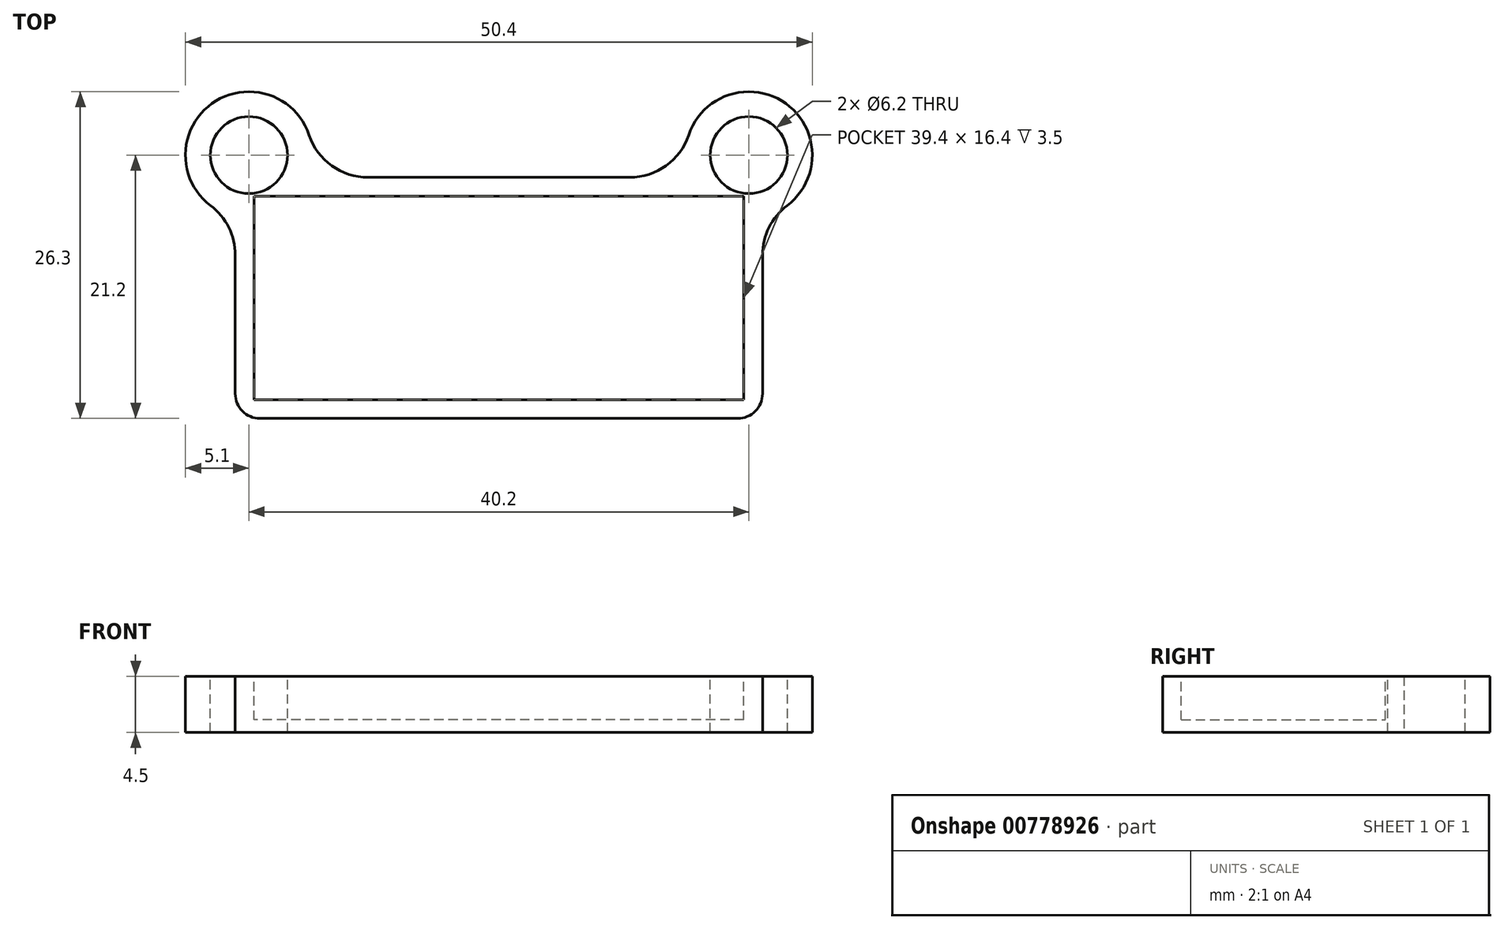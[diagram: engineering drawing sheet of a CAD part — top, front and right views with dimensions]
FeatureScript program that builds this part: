
annotation { "Feature Type Name" : "Feature", "Feature Type Description" : "" }
export const myFeature = defineFeature(function(context is Context, id is Id, definition is map)
    precondition{}
    {
        {
            var Q0;
            Q0=qCreatedBy(makeId("Top.planeOp"),FACE);
            var sketch = newSketch(context, id + "F0", { "sketchPlane" : qUnion([Q0])});
            skCircle(sketch, "E0", {"center": v(-20.1, 0) * mm, "radius": 3.1 * mm});
            skCircle(sketch, "E1", {"center": v(20.1, 0) * mm, "radius": 3.1 * mm});
            skLineSegment(sketch, "E2", {"start": v(-20.1, 0) * mm, "end": v(20.1, 0) * mm});
            skLineSegment(sketch, "E3.bottom", {"start": v(19.7, -19.7) * mm, "end": v(-19.7, -19.7) * mm});
            skLineSegment(sketch, "E3.top", {"start": v(19.7, -3.3) * mm, "end": v(-19.7, -3.3) * mm});
            skLineSegment(sketch, "E3.left", {"start": v(19.7, -19.7) * mm, "end": v(19.7, -3.3) * mm});
            skLineSegment(sketch, "E3.right", {"start": v(-19.7, -19.7) * mm, "end": v(-19.7, -3.3) * mm});
            skPoint(sketch, "E3.middle", {"position": v(0, -11.5) * mm});
            skLineSegment(sketch, "E4", {"start": v(0, 0) * mm, "end": v(0, -11.5) * mm, "construction": true});
            skSolve(sketch);
        }
        {
            var Q0;
            Q0=qCreatedBy(makeId("Top.planeOp"),FACE);
            var sketch = newSketch(context, id + "F1", { "sketchPlane" : qUnion([Q0])});
            skLineSegment(sketch, "E5.0", {"start": v(21.2, -1.8) * mm, "end": v(-21.2, -1.8) * mm});
            skLineSegment(sketch, "E5.1", {"start": v(21.2, -21.2) * mm, "end": v(21.2, -1.8) * mm});
            skLineSegment(sketch, "E5.2", {"start": v(21.2, -21.2) * mm, "end": v(-21.2, -21.2) * mm});
            skLineSegment(sketch, "E5.3", {"start": v(-21.2, -21.2) * mm, "end": v(-21.2, -1.8) * mm});
            skCircle(sketch, "E6.0", {"center": v(-20.1, 0) * mm, "radius": 5.1 * mm});
            skCircle(sketch, "E7.0", {"center": v(20.1, 0) * mm, "radius": 5.1 * mm});
            skSolve(sketch);
        }
        {
            var Q0;
            {var subQ0=sQuery(id+"F1.wireOp",EDGE,"E5.3");var subQ1=sQuery(id+"F1.wireOp",EDGE,"E5.0");var subQ2=makeQuery(id+"F1.imprint","INTERSECT",VERTEX,{"derivedFrom":[subQ1,subQ0]});Q0=makeQuery(id+"F1.imprint","IMPRINT",FACE,{"disambiguationData":[TD([[makeQuery(id+"F1.imprint","IMPRINT",EDGE,{"disambiguationData":[TD([[subQ2,1.0]])],"derivedFrom":subQ1}),-1.0]])]});}
            var Q1;
            {var subQ0=sQuery(id+"F1.wireOp",EDGE,"E5.2");Q1=makeQuery(id+"F1.imprint","IMPRINT",FACE,{"disambiguationData":[TD([[makeQuery(id+"F1.imprint","IMPRINT",EDGE,{"derivedFrom":subQ0}),-1.0]])]});}
            var Q2;
            {var subQ0=sQuery(id+"F1.wireOp",EDGE,"E5.1");var subQ1=sQuery(id+"F1.wireOp",EDGE,"E5.0");var subQ2=makeQuery(id+"F1.imprint","INTERSECT",VERTEX,{"derivedFrom":[subQ1,subQ0]});Q2=makeQuery(id+"F1.imprint","IMPRINT",FACE,{"disambiguationData":[TD([[makeQuery(id+"F1.imprint","IMPRINT",EDGE,{"disambiguationData":[TD([[subQ2,-1.0]])],"derivedFrom":subQ1}),-1.0]])]});}
            var Q3;
            {var subQ0=sQuery(id+"F1.wireOp",EDGE,"E5.1");var subQ1=sQuery(id+"F1.wireOp",EDGE,"E5.0");var subQ2=makeQuery(id+"F1.imprint","INTERSECT",VERTEX,{"derivedFrom":[subQ1,subQ0]});Q3=makeQuery(id+"F1.imprint","IMPRINT",FACE,{"disambiguationData":[TD([[makeQuery(id+"F1.imprint","IMPRINT",EDGE,{"disambiguationData":[TD([[subQ2,-1.0]])],"derivedFrom":subQ1}),1.0]])]});}
            var Q4;
            {var subQ0=sQuery(id+"F1.wireOp",EDGE,"E5.3");var subQ1=sQuery(id+"F1.wireOp",EDGE,"E5.0");var subQ2=makeQuery(id+"F1.imprint","INTERSECT",VERTEX,{"derivedFrom":[subQ1,subQ0]});Q4=makeQuery(id+"F1.imprint","IMPRINT",FACE,{"disambiguationData":[TD([[makeQuery(id+"F1.imprint","IMPRINT",EDGE,{"disambiguationData":[TD([[subQ2,1.0]])],"derivedFrom":subQ1}),1.0]])]});}
            extrude(context, id + "F2", {"entities" : qUnion([Q0, Q1, Q2, Q3, Q4]), "oppositeDirection" : true, "depth" : 4.5 * mm, "offsetDistance" : 25 * mm});
        }
        {
            var Q0;
            Q0=makeQuery(id+"F0.imprint","IMPRINT",FACE,{"disambiguationData":[TD([[makeQuery(id+"F0.imprint","IMPRINT",EDGE,{"derivedFrom":sQuery(id+"F0.wireOp",EDGE,"E0")}),1.0]])]});
            var Q1;
            Q1=makeQuery(id+"F0.imprint","IMPRINT",FACE,{"disambiguationData":[TD([[makeQuery(id+"F0.imprint","IMPRINT",EDGE,{"derivedFrom":sQuery(id+"F0.wireOp",EDGE,"E1")}),1.0]])]});
            extrude(context, id + "F3", {"entities" : qUnion([Q0, Q1]), "operationType" : NewBodyOperationType.REMOVE, "endBound" : BoundingType.THROUGH_ALL, "oppositeDirection" : true, "depth" : 25 * mm, "offsetDistance" : 25 * mm});
        }
        {
            var Q0;
            Q0=makeQuery(id+"F0.imprint","IMPRINT",FACE,{"disambiguationData":[TD([[makeQuery(id+"F0.imprint","IMPRINT",EDGE,{"derivedFrom":sQuery(id+"F0.wireOp",EDGE,"E3.bottom")}),-1.0]])]});
            extrude(context, id + "F4", {"entities" : qUnion([Q0]), "operationType" : NewBodyOperationType.REMOVE, "oppositeDirection" : true, "depth" : 3.5 * mm, "offsetDistance" : 25 * mm});
        }
        {
            var Q0;
            Q0=makeQuery(id+"F2.opExtrude","SWEPT_EDGE",EDGE,{"disambiguationData":[OSD([sQuery(id+"F1.wireOp",EDGE,"E5.2"),sQuery(id+"F1.wireOp",EDGE,"E5.3")])]});
            var Q1;
            Q1=makeQuery(id+"F2.opExtrude","SWEPT_EDGE",EDGE,{"disambiguationData":[OSD([sQuery(id+"F1.wireOp",EDGE,"E5.1"),sQuery(id+"F1.wireOp",EDGE,"E5.2")])]});
            fillet(context, id + "F5", {"entities" : qUnion([Q0, Q1]), "radius" : 2 * mm, "tangentPropagation" : true, "allowEdgeOverflow" : false});
        }
        {
            var Q0;
            Q0=makeQuery(id+"F2.opExtrude","SWEPT_EDGE",EDGE,{"disambiguationData":[OSD([sQuery(id+"F1.wireOp",EDGE,"E5.3"),sQuery(id+"F1.wireOp",EDGE,"E6.0")])]});
            var Q1;
            Q1=makeQuery(id+"F2.opExtrude","SWEPT_EDGE",EDGE,{"disambiguationData":[OSD([sQuery(id+"F1.wireOp",EDGE,"E5.0"),sQuery(id+"F1.wireOp",EDGE,"E6.0")])]});
            var Q2;
            Q2=makeQuery(id+"F2.opExtrude","SWEPT_EDGE",EDGE,{"disambiguationData":[OSD([sQuery(id+"F1.wireOp",EDGE,"E5.1"),sQuery(id+"F1.wireOp",EDGE,"E7.0")])]});
            var Q3;
            Q3=makeQuery(id+"F2.opExtrude","SWEPT_EDGE",EDGE,{"disambiguationData":[OSD([sQuery(id+"F1.wireOp",EDGE,"E5.0"),sQuery(id+"F1.wireOp",EDGE,"E7.0")])]});
            fillet(context, id + "F6", {"entities" : qUnion([Q0, Q1, Q2, Q3]), "radius" : 5 * mm, "tangentPropagation" : true, "allowEdgeOverflow" : false});
        }
    });
